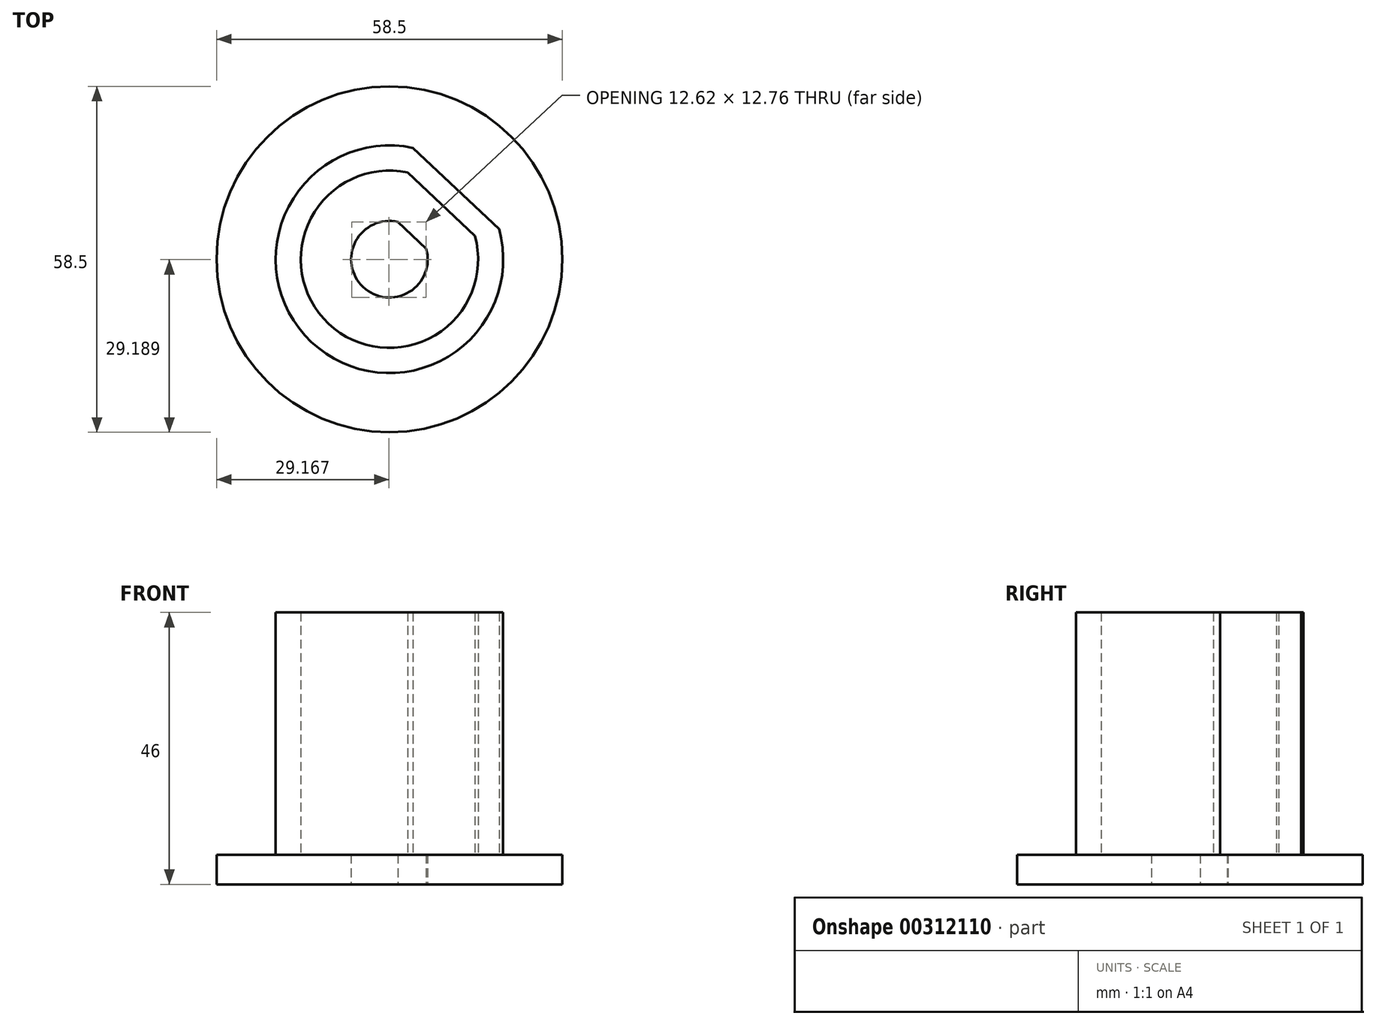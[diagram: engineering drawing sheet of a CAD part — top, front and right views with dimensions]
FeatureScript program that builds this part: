
annotation { "Feature Type Name" : "Feature", "Feature Type Description" : "" }
export const myFeature = defineFeature(function(context is Context, id is Id, definition is map)
    precondition{}
    {
        {
            var Q0;
            Q0=qCreatedBy(makeId("Top.planeOp"),FACE);
            var sketch = newSketch(context, id + "F0", { "sketchPlane" : qUnion([Q0])});
            skCircle(sketch, "E0", {"center": v(0, 0) * mm, "radius": 29.25 * mm});
            skSolve(sketch);
        }
        {
            var Q0;
            Q0 = qSketchRegion(id + "F0", true);
            extrude(context, id + "F1", {"entities" : qUnion([Q0]), "depth" : 5 * mm});
        }
        {
            var Q0;
            Q0=makeQuery(id+"F1.opExtrude","CAP_FACE",FACE,{"disambiguationData":[OSD([sQuery(id+"F0.wireOp",EDGE,"E0")])],"isStart":false});
            var sketch = newSketch(context, id + "F2", { "sketchPlane" : qUnion([Q0])});
            skArc(sketch, "E1", {"start": v(4, 18.83) * mm, "mid": v(-13.2, -14) * mm, "end": v(18.56, 5.1) * mm});
            skArc(sketch, "E2", {"start": v(3.1, 14.68) * mm, "mid": v(-10.29, -10.92) * mm, "end": v(14.47, 3.96) * mm});
            skLineSegment(sketch, "E3", {"start": v(4, 18.83) * mm, "end": v(18.56, 5.1) * mm});
            skLineSegment(sketch, "E4", {"start": v(3.1, 14.68) * mm, "end": v(14.47, 3.96) * mm});
            skSolve(sketch);
        }
        {
            var Q0;
            Q0 = qSketchRegion(id + "F2", true);
            extrude(context, id + "F3", {"entities" : qUnion([Q0]), "operationType" : NewBodyOperationType.ADD, "depth" : 41 * mm});
        }
        {
            var Q0;
            Q0=makeQuery(id+"F1.opExtrude","CAP_FACE",FACE,{"disambiguationData":[OSD([sQuery(id+"F0.wireOp",EDGE,"E0")])],"isStart":true});
            var sketch = newSketch(context, id + "F4", { "sketchPlane" : qUnion([Q0])});
            skSolve(sketch);
        }
        {
            var Q0;
            Q0=makeQuery(id+"F4.imprint","IMPRINT",FACE,{"disambiguationData":[TD([[makeQuery(id+"F4.imprint","IMPRINT",EDGE,{"derivedFrom":makeQuery(id+"F1.opExtrude","CAP_EDGE",EDGE,{"disambiguationData":[OSD([sQuery(id+"F0.wireOp",EDGE,"E0")])],"isStart":true})}),-1.0]])]});
            var sketch = newSketch(context, id + "F5", { "sketchPlane" : qUnion([Q0])});
            skArc(sketch, "E5", {"start": v(6.22, -1.79) * mm, "mid": v(-4.44, 4.71) * mm, "end": v(1.42, -6.32) * mm});
            skLineSegment(sketch, "E6", {"start": v(1.42, -6.32) * mm, "end": v(6.22, -1.79) * mm});
            skSolve(sketch);
        }
        {
            var Q0;
            Q0 = qSketchRegion(id + "F5", true);
            extrude(context, id + "F6", {"entities" : qUnion([Q0]), "operationType" : NewBodyOperationType.REMOVE, "oppositeDirection" : true, "depth" : 25.4 * mm});
        }
    });
